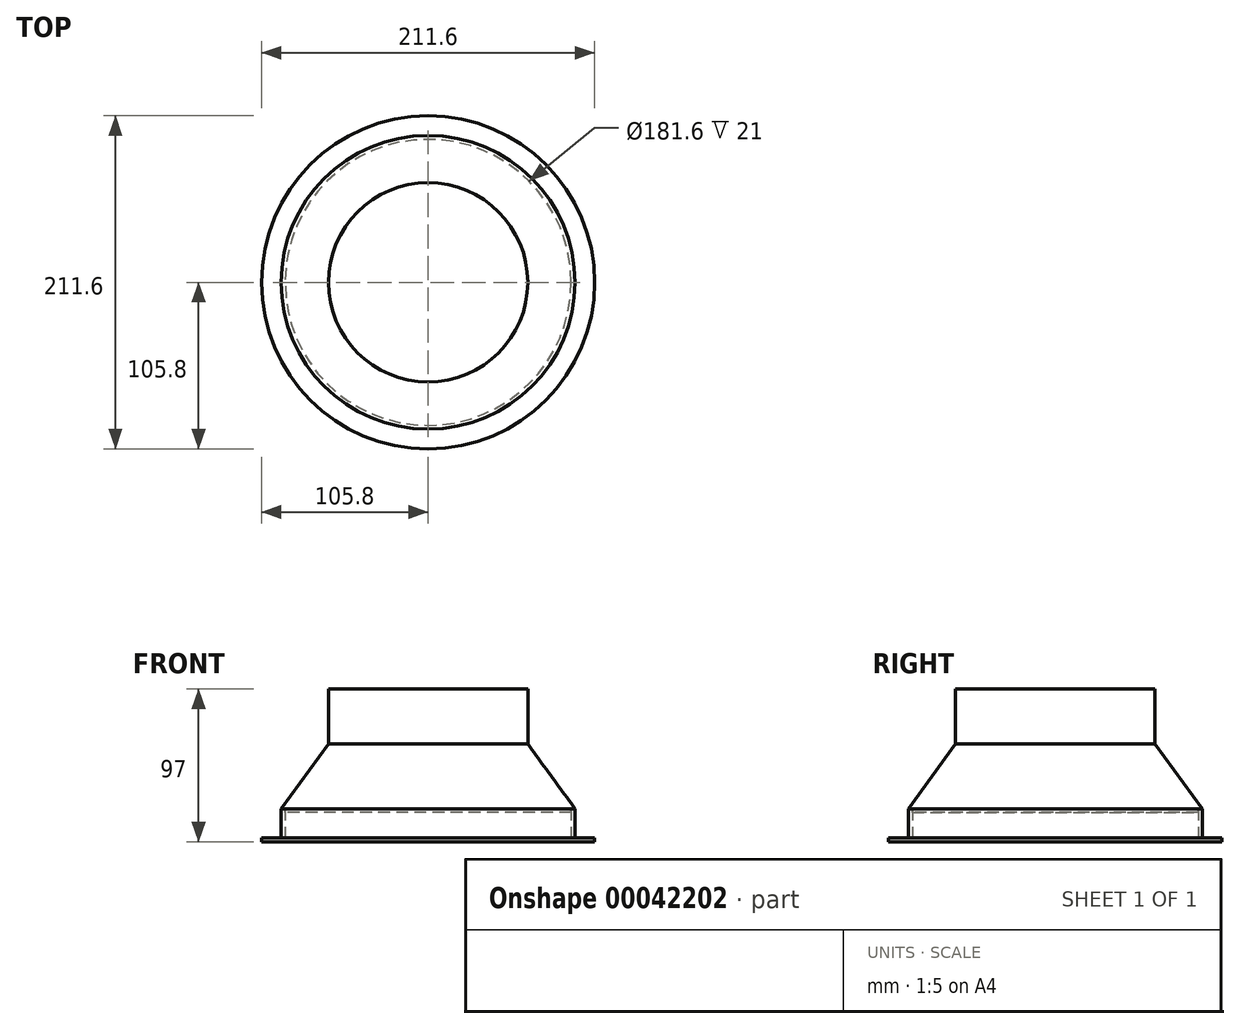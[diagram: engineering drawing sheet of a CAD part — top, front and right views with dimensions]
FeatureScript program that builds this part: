
annotation { "Feature Type Name" : "Feature", "Feature Type Description" : "" }
export const myFeature = defineFeature(function(context is Context, id is Id, definition is map)
    precondition{}
    {
        {
            var Q0;
            Q0=qCreatedBy(makeId("Top.planeOp"),FACE);
            var sketch = newSketch(context, id + "F0", { "sketchPlane" : qUnion([Q0])});
            skCircle(sketch, "E0", {"center": v(0, 0) * mm, "radius": 105.8 * mm});
            skCircle(sketch, "E1", {"center": v(0, 0) * mm, "radius": 90.8 * mm});
            skCircle(sketch, "E2", {"center": v(0, 0) * mm, "radius": 87.8 * mm});
            skCircle(sketch, "E3", {"center": v(0, 0) * mm, "radius": 93.3 * mm});
            skSolve(sketch);
        }
        {
            var Q0;
            Q0=makeQuery(id+"F0.imprint","IMPRINT",FACE,{"disambiguationData":[TD([[makeQuery(id+"F0.imprint","IMPRINT",EDGE,{"derivedFrom":sQuery(id+"F0.wireOp",EDGE,"E1")}),-1.0]])]});
            extrude(context, id + "F1", {"entities" : qUnion([Q0]), "depth" : 21 * mm});
        }
        {
            var Q0;
            Q0=makeQuery(id+"F0.imprint","IMPRINT",FACE,{"disambiguationData":[TD([[makeQuery(id+"F0.imprint","IMPRINT",EDGE,{"derivedFrom":sQuery(id+"F0.wireOp",EDGE,"E0")}),1.0]])]});
            extrude(context, id + "F2", {"entities" : qUnion([Q0]), "operationType" : NewBodyOperationType.ADD, "depth" : 2.5 * mm});
        }
        {
            var Q0;
            Q0=makeQuery(id+"F1.opExtrude","CAP_FACE",FACE,{"disambiguationData":[OSD([sQuery(id+"F0.wireOp",EDGE,"E1"),sQuery(id+"F0.wireOp",EDGE,"E3")])],"isStart":false});
            var sketch = newSketch(context, id + "F3", { "sketchPlane" : qUnion([Q0])});
            skCircle(sketch, "E4", {"center": v(0, 0) * mm, "radius": 90.8 * mm});
            skSolve(sketch);
        }
        {
            var Q0;
            Q0=makeQuery(id+"F3.imprint","IMPRINT",FACE,{"disambiguationData":[TD([[makeQuery(id+"F3.imprint","IMPRINT",EDGE,{"derivedFrom":sQuery(id+"F3.wireOp",EDGE,"E4")}),1.0]])]});
            extrude(context, id + "F4", {"entities" : qUnion([Q0]), "oppositeDirection" : true, "depth" : 2.5 * mm});
        }
        {
            var Q0;
            Q0=makeQuery(id+"F3.imprint","IMPRINT",FACE,{"disambiguationData":[TD([[makeQuery(id+"F3.imprint","IMPRINT",EDGE,{"derivedFrom":sQuery(id+"F3.wireOp",EDGE,"E4")}),1.0]])]});
            var Q1;
            Q1=makeQuery(id+"F3.imprint","IMPRINT",FACE,{"disambiguationData":[TD([[makeQuery(id+"F3.imprint","IMPRINT",EDGE,{"derivedFrom":sQuery(id+"F3.wireOp",EDGE,"E4")}),-1.0]])]});
            extrude(context, id + "F5", {"entities" : qUnion([Q0, Q1]), "depth" : 41 * mm});
        }
        {
            var Q0;
            Q0=makeQuery(id+"F5.opExtrude","CAP_EDGE",EDGE,{"disambiguationData":[OSD([sQuery(id+"F0.wireOp",EDGE,"E3")])],"isStart":false});
            chamfer(context, id + "F6", {"entities" : qUnion([Q0]), "chamferType" : ChamferType.TWO_OFFSETS, "width1" : 30 * mm, "oppositeDirection" : false, "width2" : 41 * mm, "tangentPropagation" : true});
        }
        {
            var Q0;
            Q0=makeQuery(id+"F5.opExtrude","CAP_FACE",FACE,{"disambiguationData":[OSD([sQuery(id+"F0.wireOp",EDGE,"E3")])],"isStart":false});
            extrude(context, id + "F7", {"entities" : qUnion([Q0]), "operationType" : NewBodyOperationType.ADD, "depth" : 35 * mm});
        }
    });
